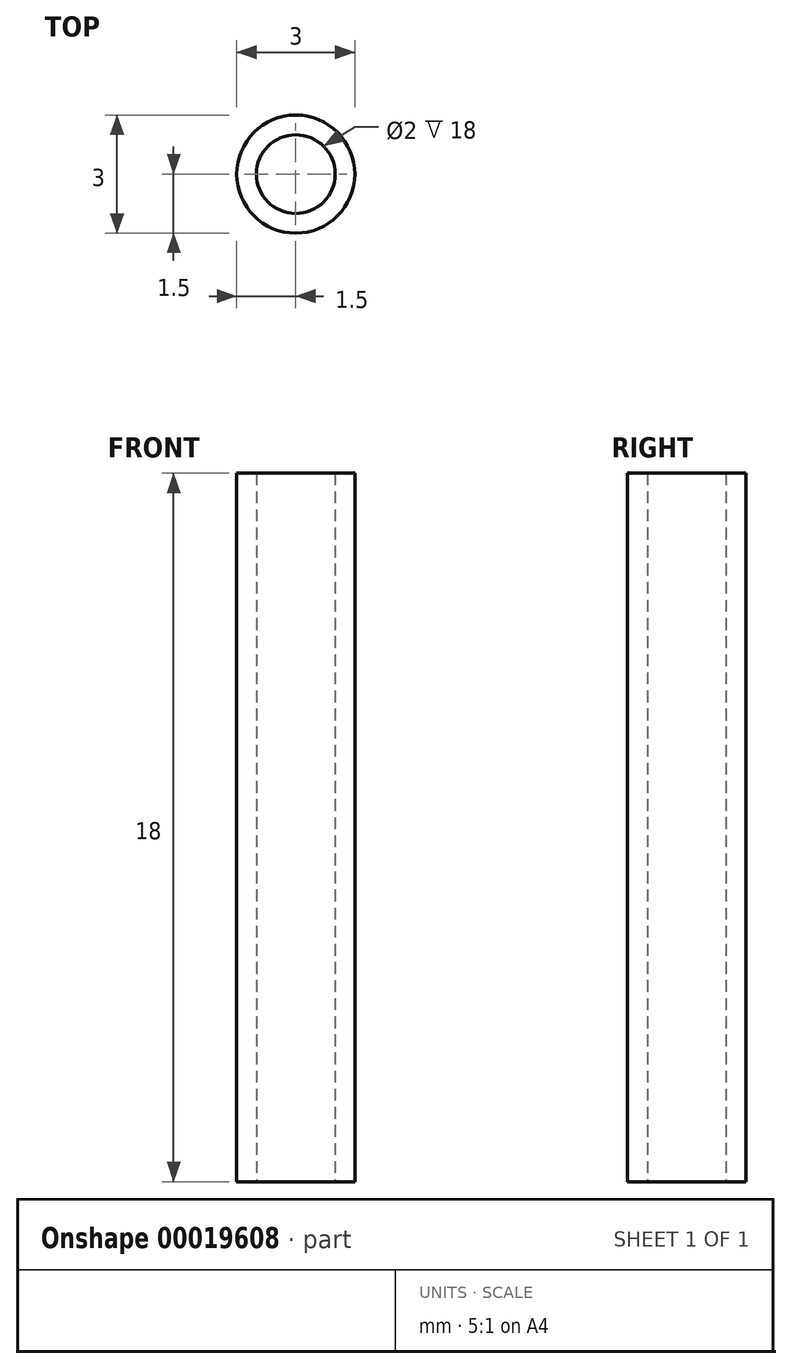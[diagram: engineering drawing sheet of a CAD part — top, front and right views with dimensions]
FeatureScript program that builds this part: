
annotation { "Feature Type Name" : "Feature", "Feature Type Description" : "" }
export const myFeature = defineFeature(function(context is Context, id is Id, definition is map)
    precondition{}
    {
        {
            var Q0;
            Q0=qCreatedBy(makeId("Top.planeOp"),FACE);
            var sketch = newSketch(context, id + "F0", { "sketchPlane" : qUnion([Q0])});
            skCircle(sketch, "E0", {"center": v(0, 0) * mm, "radius": 1 * mm});
            skCircle(sketch, "E1", {"center": v(0, 0) * mm, "radius": 1.5 * mm});
            skSolve(sketch);
        }
        {
            var Q0;
            Q0=makeQuery(id+"F0.imprint","IMPRINT",FACE,{"disambiguationData":[TD([[makeQuery(id+"F0.imprint","IMPRINT",EDGE,{"derivedFrom":sQuery(id+"F0.wireOp",EDGE,"E0")}),-1.0]])]});
            extrude(context, id + "F1", {"entities" : qUnion([Q0]), "depth" : 18 * mm});
        }
    });
